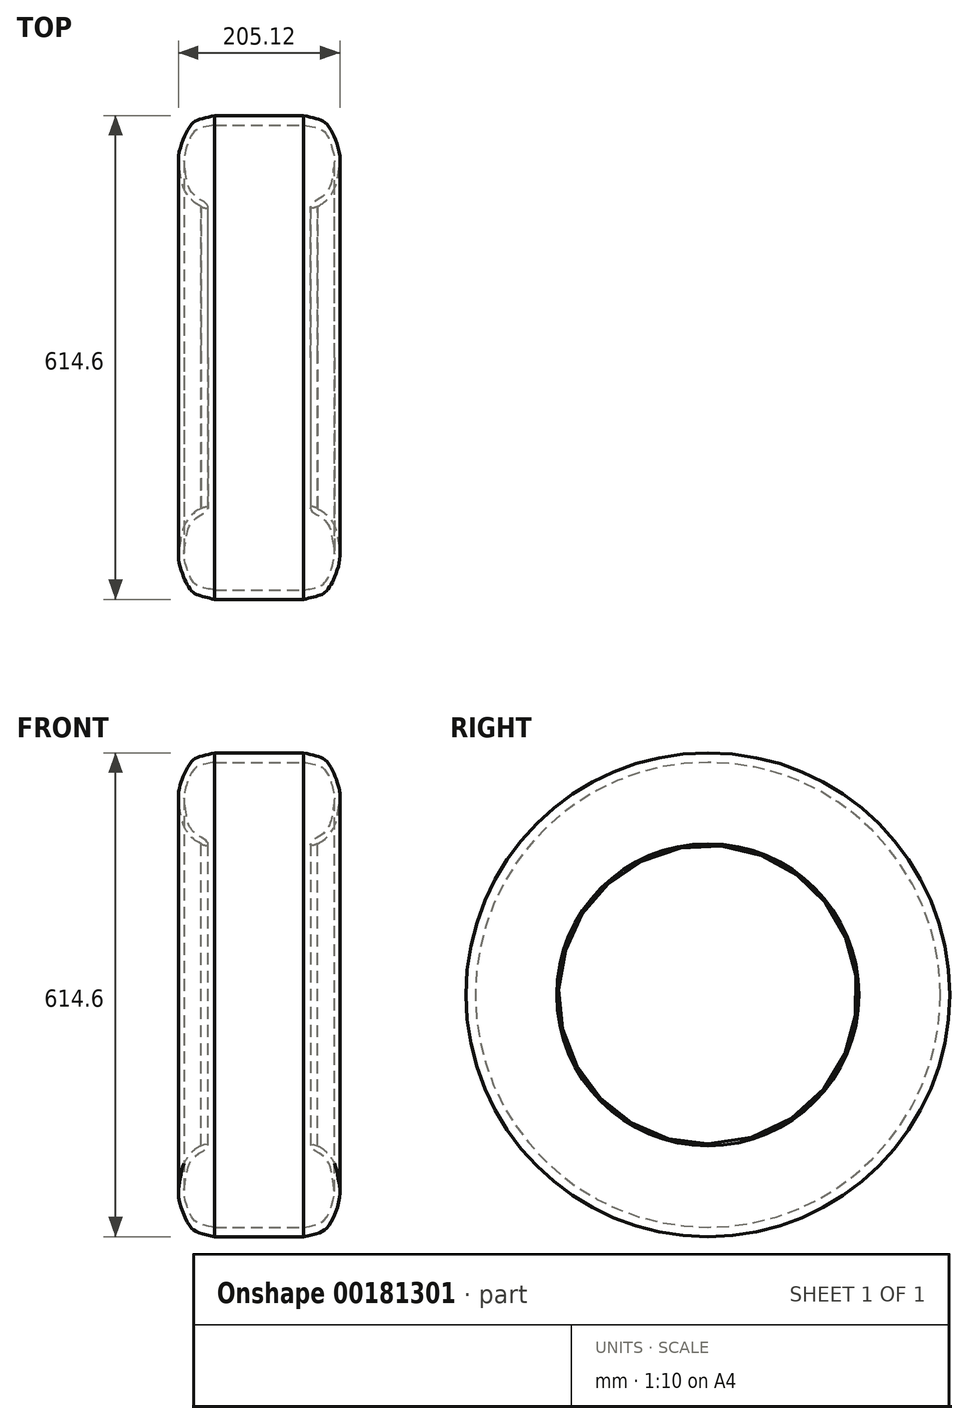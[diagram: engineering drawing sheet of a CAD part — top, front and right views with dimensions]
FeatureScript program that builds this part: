
annotation { "Feature Type Name" : "Feature", "Feature Type Description" : "" }
export const myFeature = defineFeature(function(context is Context, id is Id, definition is map)
    precondition{}
    {
        {
            var Q0;
            Q0=qCreatedBy(makeId("Front.planeOp"),FACE);
            var sketch = newSketch(context, id + "F0", { "sketchPlane" : qUnion([Q0])});
            skFitSpline(sketch, "E0", {"points": [v(74.1, 14.01) * mm, v(84.27, 20.82) * mm, v(96.04, 37.57) * mm, v(101.02, 60.21) * mm, v(101.93, 81.5) * mm, v(88.34, 115.46) * mm, v(78.38, 123.6) * mm, v(56.65, 129.5) * mm], "startDerivative": vector(91.95, 51.03) * mm, "endDerivative": vector(-163.24, 36.92) * mm});
            skLineSegment(sketch, "E1", {"start": v(0, 129.5) * mm, "end": v(56.65, 129.5) * mm});
            skLineSegment(sketch, "E2.0", {"start": v(0, -177.8) * mm, "end": v(-118.2, -177.8) * mm});
            skLineSegment(sketch, "E3.0", {"start": v(0, 117.5) * mm, "end": v(56.65, 117.5) * mm});
            skFitSpline(sketch, "E4", {"points": [v(56.65, 117.5) * mm, v(73.73, 114.01) * mm, v(83.87, 107.56) * mm, v(91.71, 90.96) * mm, v(95.4, 72.97) * mm, v(93.55, 57.3) * mm, v(90.33, 40.7) * mm, v(85.72, 31.93) * mm, v(76.95, 24.09) * mm, v(65.89, 16.25) * mm, v(65.89, 12.1) * mm, v(74.1, 14.01) * mm], "startDerivative": vector(172.3, -26.5) * mm, "endDerivative": vector(138.6, 58.5) * mm});
            skPoint(sketch, "E5.end.orphan", {"position": v(64.93, 0) * mm});
            skPoint(sketch, "E6.end.orphan", {"position": v(52.45, 0) * mm});
            skPoint(sketch, "E7.end.orphan", {"position": v(17.76, -10.13) * mm});
            skPoint(sketch, "E7.start.orphan", {"position": v(0, -10.13) * mm});
            skPoint(sketch, "E8.MirrorCS.start.orphan", {"position": v(-17.76, -10.13) * mm});
            skPoint(sketch, "E9.MirrorCS.start.orphan", {"position": v(-52.45, 0) * mm});
            skPoint(sketch, "E10.MirrorCS.start.orphan", {"position": v(-64.93, 0) * mm});
            skPoint(sketch, "E11.MirrorCS.0.internal.orphan", {"position": v(-74.1, 14.01) * mm});
            skPoint(sketch, "E12.MirrorCS.end.orphan", {"position": v(-56.65, 129.5) * mm});
            skPoint(sketch, "E12.MirrorCS.start.orphan", {"position": v(0, 129.5) * mm});
            skLineSegment(sketch, "E13.MirrorCS", {"start": v(0, 129.5) * mm, "end": v(-56.65, 129.5) * mm});
            skLineSegment(sketch, "E14.MirrorCS", {"start": v(0, 117.5) * mm, "end": v(-56.65, 117.5) * mm});
            skFitSpline(sketch, "E15.MirrorCS", {"points": [v(-56.65, 117.5) * mm, v(-73.73, 114.01) * mm, v(-83.87, 107.56) * mm, v(-91.71, 90.96) * mm, v(-95.4, 72.97) * mm, v(-93.55, 57.3) * mm, v(-90.33, 40.7) * mm, v(-85.72, 31.93) * mm, v(-76.95, 24.09) * mm, v(-65.89, 16.25) * mm, v(-65.89, 12.1) * mm, v(-74.1, 14.01) * mm], "startDerivative": vector(-172.3, -26.5) * mm, "endDerivative": vector(-138.6, 58.5) * mm});
            skFitSpline(sketch, "E16.MirrorCS", {"points": [v(-74.1, 14.01) * mm, v(-84.27, 20.82) * mm, v(-96.04, 37.57) * mm, v(-101.02, 60.21) * mm, v(-101.93, 81.5) * mm, v(-88.34, 115.46) * mm, v(-78.38, 123.6) * mm, v(-56.65, 129.5) * mm], "startDerivative": vector(-91.95, 51.03) * mm, "endDerivative": vector(163.24, 36.92) * mm});
            skSolve(sketch);
        }
        {
            var Q0;
            Q0=qSketchRegion(id+"F0",true);
            var Q1;
            Q1=sQuery(id+"F0.wireOp",EDGE,"E2.0");
            revolve(context, id + "F1", {"entities" : qUnion([Q0]), "axis" : qUnion([Q1]), "revolveType" : RevolveType.FULL});
        }
    });
